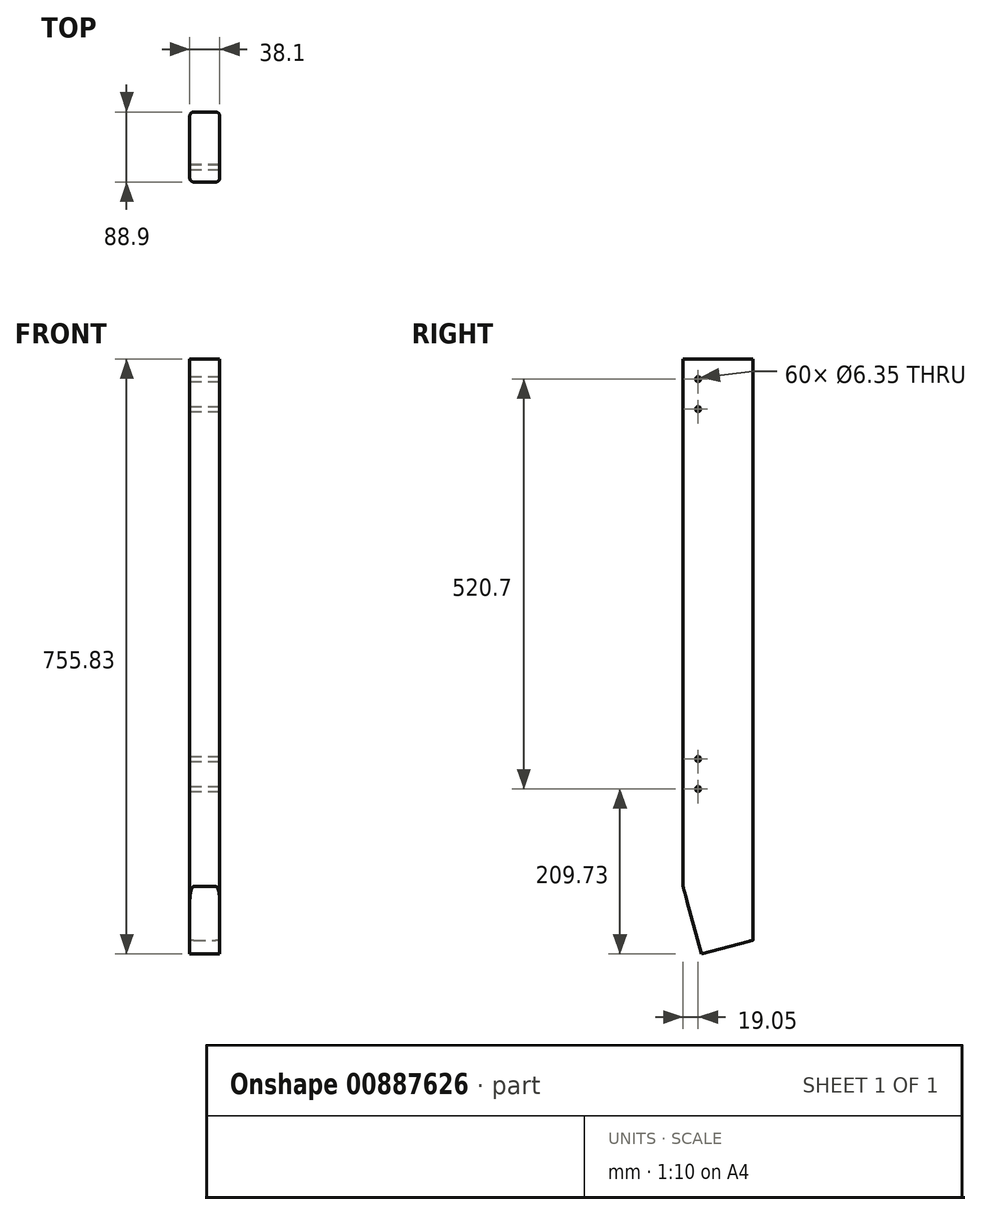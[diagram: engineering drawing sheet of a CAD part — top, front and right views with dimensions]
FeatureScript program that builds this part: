
annotation { "Feature Type Name" : "Feature", "Feature Type Description" : "" }
export const myFeature = defineFeature(function(context is Context, id is Id, definition is map)
    precondition{}
    {
        {
            var Q0;
            Q0=qCreatedBy(makeId("Top.planeOp"),FACE);
            var sketch = newSketch(context, id + "F0", { "sketchPlane" : qUnion([Q0])});
            skLineSegment(sketch, "E0.bottom", {"start": v(19.05, 44.45) * mm, "end": v(-19.05, 44.45) * mm});
            skLineSegment(sketch, "E0.top", {"start": v(19.05, -44.45) * mm, "end": v(-19.05, -44.45) * mm});
            skLineSegment(sketch, "E0.left", {"start": v(19.05, 44.45) * mm, "end": v(19.05, -44.45) * mm});
            skLineSegment(sketch, "E0.right", {"start": v(-19.05, 44.45) * mm, "end": v(-19.05, -44.45) * mm});
            skPoint(sketch, "E0.middle", {"position": v(0, 0) * mm});
            skSolve(sketch);
        }
        {
            var Q0;
            Q0=makeQuery(id+"F0.imprint","IMPRINT",FACE,{"disambiguationData":[TD([[makeQuery(id+"F0.imprint","IMPRINT",EDGE,{"derivedFrom":sQuery(id+"F0.wireOp",EDGE,"E0.bottom")}),1.0]])]});
            extrude(context, id + "F1", {"entities" : qUnion([Q0]), "endBound" : BoundingType.SYMMETRIC, "depth" : 762 * mm, "offsetDistance" : 25.4 * mm});
        }
        {
            var Q0;
            Q0=makeQuery(id+"F1.opExtrude","SWEPT_FACE",FACE,{"disambiguationData":[OSD([sQuery(id+"F0.wireOp",EDGE,"E0.left")])]});
            var sketch = newSketch(context, id + "F2", { "sketchPlane" : qUnion([Q0])});
            skLineSegment(sketch, "E1", {"start": v(-44.45, -381) * mm, "end": v(44.45, -381) * mm});
            skLineSegment(sketch, "E2", {"start": v(44.45, -381) * mm, "end": v(44.45, -357.18) * mm});
            skLineSegment(sketch, "E3", {"start": v(44.45, -357.18) * mm, "end": v(-44.45, -381) * mm});
            skLineSegment(sketch, "E4", {"start": v(-21.44, -374.83) * mm, "end": v(-44.45, -288.96) * mm});
            skSolve(sketch);
        }
        {
            var Q0;
            Q0=makeQuery(id+"F2.imprint","IMPRINT",FACE,{"disambiguationData":[TD([[makeQuery(id+"F2.imprint","IMPRINT",EDGE,{"derivedFrom":sQuery(id+"F2.wireOp",EDGE,"3avJKaC2-YBW0-gP52-5ExU-NXhLxU1TCf7H")}),-1.0]])]});
            var Q1;
            Q1=makeQuery(id+"F2.imprint","IMPRINT",FACE,{"disambiguationData":[TD([[makeQuery(id+"F2.imprint","IMPRINT",EDGE,{"derivedFrom":sQuery(id+"F2.wireOp",EDGE,"E1")}),-1.0]])]});
            var Q2;
            {var subQ3=sQuery(id+"F2.wireOp",EDGE,"E4");Q2=makeQuery(id+"F2.imprint","IMPRINT",FACE,{"disambiguationData":[TD([[makeQuery(id+"F2.imprint","IMPRINT",EDGE,{"derivedFrom":subQ3}),1.0]])]});}
            extrude(context, id + "F3", {"entities" : qUnion([Q0, Q1, Q2]), "operationType" : NewBodyOperationType.REMOVE, "endBound" : BoundingType.THROUGH_ALL, "oppositeDirection" : true, "depth" : 25.4 * mm, "offsetDistance" : 25.4 * mm});
        }
        {
            var Q0;
            Q0=makeQuery(id+"F1.opExtrude","SWEPT_EDGE",EDGE,{"disambiguationData":[OSD([sQuery(id+"F0.wireOp",EDGE,"E0.top"),sQuery(id+"F0.wireOp",EDGE,"E0.left")])]});
            var Q1;
            Q1=makeQuery(id+"F1.opExtrude","SWEPT_EDGE",EDGE,{"disambiguationData":[OSD([sQuery(id+"F0.wireOp",EDGE,"E0.top"),sQuery(id+"F0.wireOp",EDGE,"E0.right")])]});
            var Q2;
            Q2=makeQuery(id+"F1.opExtrude","SWEPT_EDGE",EDGE,{"disambiguationData":[OSD([sQuery(id+"F0.wireOp",EDGE,"E0.bottom"),sQuery(id+"F0.wireOp",EDGE,"E0.left")])]});
            var Q3;
            Q3=makeQuery(id+"F1.opExtrude","SWEPT_EDGE",EDGE,{"disambiguationData":[OSD([sQuery(id+"F0.wireOp",EDGE,"E0.bottom"),sQuery(id+"F0.wireOp",EDGE,"E0.right")])]});
            fillet(context, id + "F4", {"entities" : qUnion([Q0, Q1, Q2, Q3]), "radius" : 5.08 * mm, "tangentPropagation" : true, "allowEdgeOverflow" : false});
        }
        {
            var Q0;
            Q0=makeQuery(id+"F1.opExtrude","SWEPT_FACE",FACE,{"disambiguationData":[OSD([sQuery(id+"F0.wireOp",EDGE,"E0.left")])]});
            var sketch = newSketch(context, id + "F5", { "sketchPlane" : qUnion([Q0])});
            skPoint(sketch, "E5", {"position": v(-25.4, 355.6) * mm});
            skPoint(sketch, "E6", {"position": v(-25.4, 317.5) * mm});
            skPoint(sketch, "E7", {"position": v(-25.4, -127) * mm});
            skPoint(sketch, "E8", {"position": v(-25.4, -165.1) * mm});
            skSolve(sketch);
        }
        {
            var Q0;
            Q0=sQuery(id+"F5.wireOp",VERTEX,"E5");
            var Q1;
            Q1=sQuery(id+"F5.wireOp",VERTEX,"E6");
            var Q2;
            Q2=sQuery(id+"F5.wireOp",VERTEX,"E7");
            var Q3;
            Q3=sQuery(id+"F5.wireOp",VERTEX,"E8");
            var Q4;
            Q4=makeQuery(id+"F1.opExtrude","SWEPT_BODY",BODY,{"disambiguationData":[OSD([sQuery(id+"F0.wireOp",EDGE,"E0.bottom"),sQuery(id+"F0.wireOp",EDGE,"E0.top"),sQuery(id+"F0.wireOp",EDGE,"E0.left"),sQuery(id+"F0.wireOp",EDGE,"E0.right")])]});
            hole(context, id + "F6", {"style" : HoleStyle.SIMPLE, "endStyle" : HoleEndStyle.THROUGH, "holeDiameter" : 6.35 * mm, "majorDiameter" : 6.35 * mm, "isTappedThrough" : true, "tappedDepth" : 12.7 * mm, "tapClearance" : 3, "locations" : qUnion([Q0, Q1, Q2, Q3]), "scope" : qUnion([Q4])});
        }
    });
